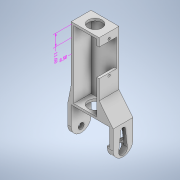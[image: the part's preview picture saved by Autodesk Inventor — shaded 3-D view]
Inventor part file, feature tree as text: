
AUTODESK INVENTOR PART (.ipt)
format: ipt  version: 2022.2 (Build 262287010, 287A)  size: 278,016 bytes
history: native  units: mm
features: extrude x13, sketch x13, other x3, fillet x1
ambient origin geometry x8: Origin, YZ Plane, XZ Plane, XY Plane, X Axis, Y Axis, Z Axis, Center Point
bodies: Solid1 (feature_tree)
feature tree (30):
  other  "Annotations"
  extrude  "Extrusion1"  Depth=60.0mm
  extrude  "Extrusion2"  Depth=2.0mm
  extrude  "Extrusion3"  Depth=15.0mm TaperAngle=0.0deg
  extrude  "Extrusion4"  Depth=2.0mm
  extrude  "Extrusion5"  Depth=8.5mm
  extrude  "Extrusion9"  Depth=3.0mm
  extrude  "Extrusion10"  Depth=15.0mm
  extrude  "Extrusion11"  Depth=2.0mm
  extrude  "Extrusion12"  Depth=15.0mm TaperAngle=0.0deg
  extrude  "Extrusion13"  Depth=5.0mm TaperAngle=0.0deg
  extrude  "Extrusion14"  TaperAngle=0.0deg  [1 undecoded]
  fillet  "Fillet2"  Radius=3.0mm
  extrude  "Extrusion15"  TaperAngle=0.0deg  [1 undecoded]
  extrude  "Extrusion16"  Depth=5.0mm
  sketch  "Sketch1"  dims[d0=24.0mm d1=60.0mm]
  sketch  "Sketch2"  dims[d2=2.0mm d3=0.0mm d4=2.0mm]
  sketch  "Sketch3"  dims[d5=2.0mm d6=15.0mm d7=0.0mm]
  sketch  "Sketch4"  dims[d8=2.0mm d9=2.0mm]
  sketch  "Sketch5"  dims[d10=8.5mm d11=8.5mm]
  sketch  "Sketch12"  dims[d12=27.5mm d13=3.0mm]
  sketch  "Sketch13"  dims[d14=12.0mm d15=0.0mm d23=15.0mm]
  sketch  "Sketch14"  dims[d24=23.5mm d25=2.0mm]
  sketch  "Sketch15"  dims[d26=2.0mm d27=15.0mm d28=0.0mm]
  sketch  "Sketch16"  dims[d29=5.0mm d30=5.0mm d31=0.0mm]
  sketch  "Sketch17"  dims[d32=8.6mm d33=0.0mm d52=3.0mm]
  sketch  "Sketch18"  dims[d53=25.0mm d54=0.0mm]
  sketch  "Sketch20"  dims[d55=3.0mm d56=5.0mm d57=10.0mm d58=0.0mm d59=15.0mm d60=90.0deg d61=10.0mm d62=0.0mm d63=15.0mm d64=90.0deg d65=5.0mm d66=8.5mm d67=20.0mm d68=20.0mm d69=0.0mm d70=2.0mm d71=0.0mm d72=2.0mm d73=0.0mm d74=12.0mm d75=12.0mm d76=8.5mm d77=46.5mm d78=0.0mm d79=8.5mm d80=7.5mm d81=10.0mm d82=0.0mm d83=31.0mm d84=4.0mm d85=15.0mm d86=0.0mm d87=3.0mm d88=0.0mm d89=4.0mm d90=15.0mm d91=0.0mm d92=2.0mm d93=15.0mm d36=6.779666mm d37=11.6mm d43=1.279577mm d44=8.5mm d94=0.5mm d95=0.872665mm]
  other  "Linear Dimension 1"
  other  "Linear Dimension 3"
note: 2 required parameter values undecoded (feature->parameter linkage not recoverable at this tier; creation-order binding heuristic only, values carry confidence <= 0.55)
